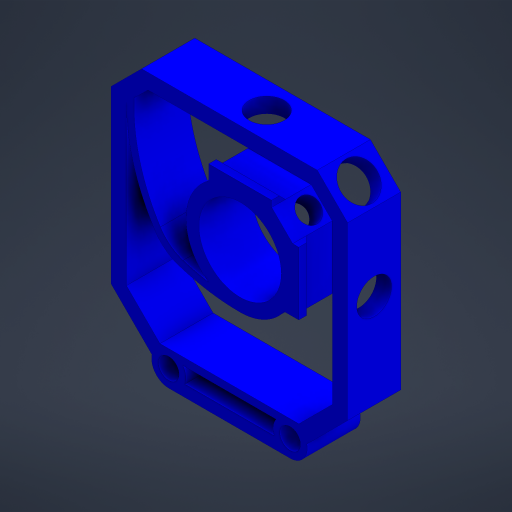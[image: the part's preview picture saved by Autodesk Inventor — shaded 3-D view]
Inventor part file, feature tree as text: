
AUTODESK INVENTOR PART (.ipt)
format: ipt  version: 2023.4 (Build 274418000, 418)  size: 439,808 bytes
history: native  units: mm
features: extrude x6, reference x4, projected_geometry x3, other x3, plane x1, mirror x1, sketch x1
ambient origin geometry x8: Origin, YZ Plane, XZ Plane, XY Plane, X Axis, Y Axis, Z Axis, Center Point
bodies: Solid1 (feature_tree)
feature tree (19):
  extrude  "Extrusion1"  TaperAngle=45.0deg  [1 undecoded]
  extrude  "Extrusion2"  Depth=10.0mm
  extrude  "Extrusion3"  Depth=10.0mm
  extrude  "Extrusion4"  Depth=10.0mm
  plane  "Work Plane1"
  mirror  "Mirror1"
  extrude  "Extrusion5"  Depth=10.0mm
  extrude  "Extrusion6"  Depth=10.0mm
  sketch  "Sketch1"  dims[d2=2.5mm d3=45.0deg d4=13.5675mm d5=0.675mm d6=2.125mm d7=0.5mm d8=10.375mm d9=2.5mm d10=0.625mm d11=5.0mm d12=135.0deg d13=3.0mm d14=2.0mm d15=2.0mm d16=38.935534mm d17=38.935534mm d18=9.25mm d19=9.25mm d20=9.25mm d21=9.25mm d22=5.0mm d23=5.0mm d24=5.0mm d25=5.0mm d26=2.5mm d28=8.75mm d29=0.0mm d30=0.875mm d31=0.875mm d32=0.0mm d33=5.75mm d34=10.0mm d35=0.0mm d36=1.25mm d37=135.0deg d38=10.0mm d39=0.0mm d40=3.75mm d41=6.0mm d42=5.0mm d43=0.0mm d44=10.0mm d45=0.0mm d46=2.5mm d50=12.5mm d51=2.5mm d52=1.25mm d53=2.5mm d54=2.5mm d55=0.1425mm d56=0.1425mm d57=1.25mm d58=1.25mm]
  projected_geometry  "Projected Loop1"
  projected_geometry  "Projected Loop2"
  projected_geometry  "Projected Loop4"
  reference  "Reference4"
  reference  "Reference5"
  reference  "Reference6"
  reference  "Reference7"
  other  "<path>\Projects\Project Protocube\Protocube\CAD, STL, OBJ Files\1 CAD\Cube 1x1 V5.iam"
  other  "Cube 1x1 V5.iam"
  other  "Cube 1x1 Bottom V5 Closed Slotted:1"
note: 1 required parameter value undecoded (feature->parameter linkage not recoverable at this tier; creation-order binding heuristic only, values carry confidence <= 0.55)
note: 1 file-system path scrubbed to <path> (originals preserved in map.json)
